# Revit family: IS_CeraplanNew_B4277_BIM_BE
name_source: partatom
category: Plumbing Fixtures
revit_build: Autodesk Revit 2015 (Build: 20140606_1530(x64)
units: mm (PartAtom-declared; Revit-internal decimal feet)

## types (1)
- B4277AA - Ceraplan New Mitigeur cuisine avec bec haut ECO
    Accesoires = www.idealstandard.be
    Afwerking = Chroom
    Auteur = Ideal Standard Produktions-GmbH
    Barcode = 3800019245334
    Bedieningkraan = manueel met greep
    Bedieningkraanwerk = eengreeps
    Beschrijvinggarantie = Fabrieksgarantie
    BimObjectNaam = ISI_IdealStandard_Mitigeur_Ceraplan_B4277AA
    Breedte = 0
    BrutoGewicht = 0
    Cost = 0 $
    Debiet = 13L/min | 3bar
    Default Elevation = 1219 mm
    Description = Ceraplan New Mitigeur cuisine avec bec haut ECO
    Diepte = 0 mm  [stored 0 ft]
    Dimensions = 238 x 98 x 321 mm
    DuurEenheid = jaar
    Eigenschappen = CeraPlan New keukenmengkraan DN 15 met hoge uitloop. Beweegbare uitloop en perlator. Sprong 200 mm. Hoogte uitloop 180 mm. Flexibele aansluitleidingen G3/8. Metalen greep. Onderbevestiging  (EASY FIX). Kraangat Ø34 mm. CLICK-cartouche met keramische schijven. Bevestiging greep op de cartouche dmv een RVS overbrengingspen. Draaibereik 120°. Geïntegreerd vetreservoir. Geïntegreerde temperatuurbegrenzer en ECO-functie. Uithoudingstest EN 817. Geluidsniveau volgens norm DIN 4109, Groep 1.
    Garantieonderdelen = 5
    Hauteur = 321 mm
    IfcExportAs = IfcValveTypes
    IfcExportType = TAPS
    Installatieinstructies = www.idealstandard.be
    Kleur = Chroom
    Largeur = 98 mm
    Lengte = 0 mm  [stored 0 ft]
    Longueur = 238 mm
    Manufacturer = www.idealstandard.be
    Materiaal = messing verchroomd
    Merk = Ideal Standard
    Model = B4277AA
    Nettogewicht = 1.3
    Normen = EN 817
DIN 4109
    Productinformatie = www.idealstandard.be
    Telefoonnummer = 0032 2 325 66 00
    Testdruk = 10 bar
    Typeconnectie = Sanitair
    Typekraanwerk = keuken
    URL = www.idealstandard.be
    Uniclass2015Beschrijving = Sink taps
    Uniclass2015Referentie = Pr_40_20_87_84
    Uniclass2015Version = Products v1.1
    Urlproducent = www.idealstandard.be
    Versie = 1
    Vervangingskosten = 0
    Verwachtelevensduur = 25 jaar
    Volumeunits = liter
    Werkdruk = 1-5 bar

note: [stored X ft] marks values corroborated as IEEE doubles in the binary element streams (Revit-internal decimal feet)

## geometry (parser evidence)
native form markers: Blend x2, Sweep x3
no freeform markers — native parametric forms only
